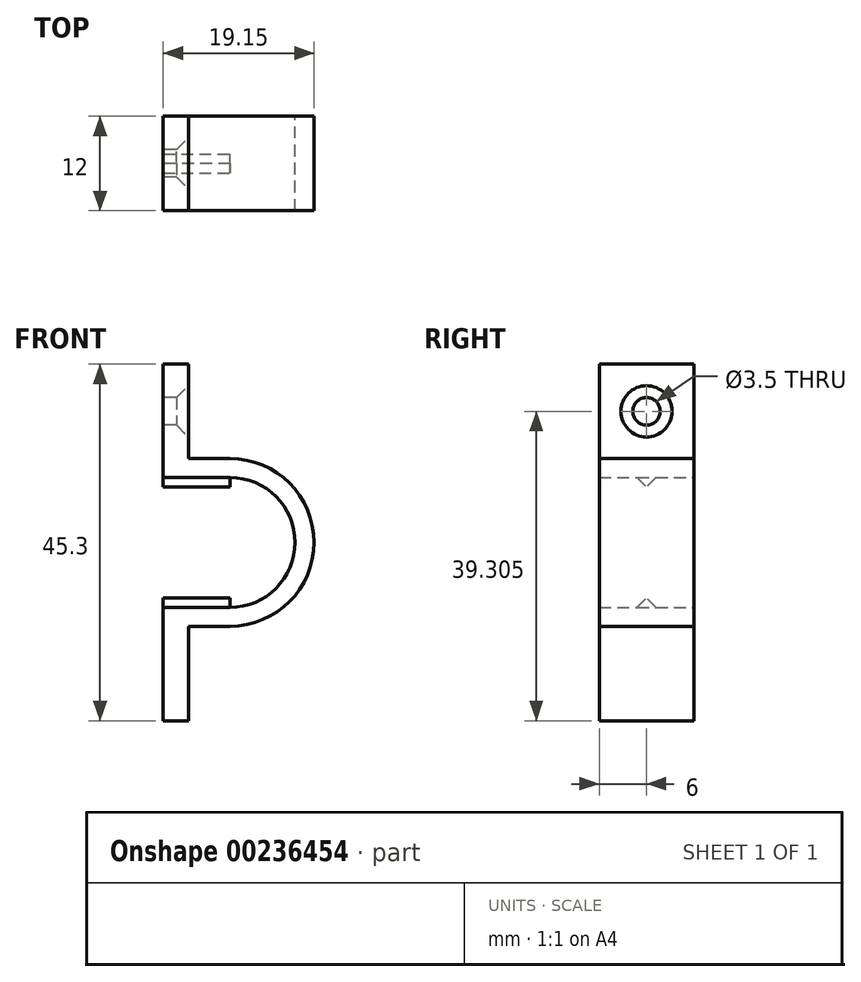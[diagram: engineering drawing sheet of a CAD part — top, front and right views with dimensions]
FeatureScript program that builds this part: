
annotation { "Feature Type Name" : "Feature", "Feature Type Description" : "" }
export const myFeature = defineFeature(function(context is Context, id is Id, definition is map)
    precondition{}
    {
        {
            var Q0;
            Q0=qCreatedBy(makeId("Front.planeOp"),FACE);
            var sketch = newSketch(context, id + "F0", { "sketchPlane" : qUnion([Q0])});
            skLineSegment(sketch, "E0.bottom", {"start": v(-39.03, 42) * mm, "end": v(-35.83, 42) * mm});
            skLineSegment(sketch, "E0.top", {"start": v(-39.03, -3.3) * mm, "end": v(-35.83, -3.3) * mm});
            skLineSegment(sketch, "E0.left", {"start": v(-39.03, 42) * mm, "end": v(-39.03, 27.6) * mm});
            skLineSegment(sketch, "E0.right", {"start": v(-35.83, 42) * mm, "end": v(-35.83, 30) * mm});
            skLineSegment(sketch, "E1.trimOffspring", {"start": v(-35.83, 8.7) * mm, "end": v(-35.83, -3.3) * mm});
            skLineSegment(sketch, "E2.trimOffspring", {"start": v(-39.03, 11.1) * mm, "end": v(-39.03, -3.3) * mm});
            skLineSegment(sketch, "E3", {"start": v(-35.83, 30) * mm, "end": v(-30.53, 30) * mm});
            skLineSegment(sketch, "E4", {"start": v(-30.53, 27.6) * mm, "end": v(-39.03, 27.6) * mm});
            skLineSegment(sketch, "E5", {"start": v(-39.03, 11.1) * mm, "end": v(-30.53, 11.1) * mm});
            skLineSegment(sketch, "E6", {"start": v(-30.53, 8.7) * mm, "end": v(-35.83, 8.7) * mm});
            skLineSegment(sketch, "E7", {"start": v(-30.53, 27.6) * mm, "end": v(-30.53, 11.1) * mm, "construction": true});
            skArc(sketch, "E8", {"start": v(-30.53, 11.1) * mm, "mid": v(-22.28, 19.34) * mm, "end": v(-30.53, 27.6) * mm});
            skArc(sketch, "E9", {"start": v(-30.53, 8.7) * mm, "mid": v(-19.88, 19.34) * mm, "end": v(-30.53, 30) * mm});
            skSolve(sketch);
        }
        {
            var Q0;
            Q0=makeQuery(id+"F0.imprint","IMPRINT",FACE,{"disambiguationData":[TD([[makeQuery(id+"F0.imprint","IMPRINT",EDGE,{"derivedFrom":sQuery(id+"F0.wireOp",EDGE,"E0.bottom")}),-1.0]])]});
            extrude(context, id + "F1", {"entities" : qUnion([Q0]), "depth" : 12 * mm});
        }
        {
            var Q0;
            Q0=makeQuery(id+"F1.opExtrude","SWEPT_FACE",FACE,{"disambiguationData":[OSD([sQuery(id+"F0.wireOp",EDGE,"E0.left")])]});
            var sketch = newSketch(context, id + "F2", { "sketchPlane" : qUnion([Q0])});
            skCircle(sketch, "E10", {"center": v(6, 36) * mm, "radius": 1.75 * mm});
            skLineSegment(sketch, "E11.0.0", {"start": v(0, 11.1) * mm, "end": v(0, 27.6) * mm, "construction": true});
            skLineSegment(sketch, "E11.0.1", {"start": v(0, 11.1) * mm, "end": v(12, 11.1) * mm, "construction": true});
            skLineSegment(sketch, "E11.0.2", {"start": v(12, 11.1) * mm, "end": v(12, 27.6) * mm, "construction": true});
            skLineSegment(sketch, "E11.0.3", {"start": v(12, 27.6) * mm, "end": v(0, 27.6) * mm, "construction": true});
            skLineSegment(sketch, "E12", {"start": v(0, 19.34) * mm, "end": v(12, 19.34) * mm, "construction": true});
            skCircle(sketch, "E13.MirrorC", {"center": v(6, 2.7) * mm, "radius": 1.75 * mm});
            skSolve(sketch);
        }
        {
            var Q0;
            Q0=makeQuery(id+"F2.imprint","IMPRINT",FACE,{"disambiguationData":[TD([[makeQuery(id+"F2.imprint","IMPRINT",EDGE,{"derivedFrom":sQuery(id+"F2.wireOp",EDGE,"E10")}),1.0]])]});
            var Q1;
            Q1=makeQuery(id+"F2.imprint","IMPRINT",FACE,{"disambiguationData":[TD([[makeQuery(id+"F2.imprint","IMPRINT",EDGE,{"derivedFrom":sQuery(id+"F2.wireOp",EDGE,"E13.MirrorC")}),-1.0]])]});
            extrude(context, id + "F3", {"entities" : qUnion([Q0, Q1]), "operationType" : NewBodyOperationType.REMOVE, "endBound" : BoundingType.THROUGH_ALL, "oppositeDirection" : true, "depth" : 25 * mm});
        }
        {
            var Q0;
            Q0=makeQuery(id+"F3.boolean.opBoolean","INTERSECT",EDGE,{"derivedFrom":[makeQuery(id+"F1.opExtrude","SWEPT_FACE",FACE,{"disambiguationData":[OSD([sQuery(id+"F0.wireOp",EDGE,"E0.right")])]}),makeQuery(id+"F3.opExtrude","SWEPT_FACE",FACE,{"disambiguationData":[OSD([sQuery(id+"F2.wireOp",EDGE,"E10")])]})]});
            var Q1;
            Q1=makeQuery(id+"F3.boolean.opBoolean","INTERSECT",EDGE,{"derivedFrom":[makeQuery(id+"F1.opExtrude","SWEPT_FACE",FACE,{"disambiguationData":[OSD([sQuery(id+"F0.wireOp",EDGE,"E1.trimOffspring")])]}),makeQuery(id+"F3.opExtrude","SWEPT_FACE",FACE,{"disambiguationData":[OSD([sQuery(id+"F2.wireOp",EDGE,"E13.MirrorC")])]})]});
            chamfer(context, id + "F4", {"entities" : qUnion([Q0, Q1]), "width" : 1.5 * mm, "tangentPropagation" : true});
        }
        {
            var Q0;
            Q0=makeQuery(id+"F1.opExtrude","SWEPT_FACE",FACE,{"disambiguationData":[OSD([sQuery(id+"F0.wireOp",EDGE,"E5")])]});
            var sketch = newSketch(context, id + "F5", { "sketchPlane" : qUnion([Q0])});
            skLineSegment(sketch, "E14", {"start": v(-30.53, -6) * mm, "end": v(-39.03, -6) * mm, "construction": true});
            skLineSegment(sketch, "E15.bottom", {"start": v(-39.03, -7.2) * mm, "end": v(-30.53, -7.2) * mm});
            skLineSegment(sketch, "E15.top", {"start": v(-39.03, -4.8) * mm, "end": v(-30.53, -4.8) * mm});
            skLineSegment(sketch, "E15.left", {"start": v(-39.03, -7.2) * mm, "end": v(-39.03, -4.8) * mm});
            skPoint(sketch, "E15.middle", {"position": v(-30.53, -6) * mm});
            skLineSegment(sketch, "E16", {"start": v(-30.53, -4.8) * mm, "end": v(-30.53, -7.2) * mm});
            skPoint(sketch, "E15.right.end.orphan", {"position": v(-22.03, -4.8) * mm});
            skPoint(sketch, "E17.orphan", {"position": v(-22.03, -7.2) * mm});
            skSolve(sketch);
        }
        {
            var Q0;
            {var subQ0=sQuery(id+"F5.wireOp",EDGE,"E15.left");Q0=makeQuery(id+"F5.imprint","IMPRINT",FACE,{"disambiguationData":[TD([[makeQuery(id+"F5.imprint","IMPRINT",EDGE,{"derivedFrom":subQ0}),-1.0]])]});}
            extrude(context, id + "F6", {"entities" : qUnion([Q0]), "operationType" : NewBodyOperationType.ADD, "depth" : 1.2 * mm});
        }
        {
            var Q0;
            Q0=makeQuery(id+"F1.opExtrude","SWEPT_FACE",FACE,{"disambiguationData":[OSD([sQuery(id+"F0.wireOp",EDGE,"E4")])]});
            var sketch = newSketch(context, id + "F7", { "sketchPlane" : qUnion([Q0])});
            skLineSegment(sketch, "E18.bottom", {"start": v(-39.03, 4.8) * mm, "end": v(-30.53, 4.8) * mm});
            skLineSegment(sketch, "E18.top", {"start": v(-39.03, 7.2) * mm, "end": v(-30.53, 7.2) * mm});
            skLineSegment(sketch, "E18.left", {"start": v(-39.03, 4.8) * mm, "end": v(-39.03, 7.2) * mm});
            skPoint(sketch, "E18.middle", {"position": v(-30.53, 6) * mm});
            skLineSegment(sketch, "E19", {"start": v(-30.53, 7.2) * mm, "end": v(-30.53, 4.8) * mm});
            skPoint(sketch, "E18.right.end.orphan", {"position": v(-22.03, 7.2) * mm});
            skPoint(sketch, "E18.right.start.orphan", {"position": v(-22.03, 4.8) * mm});
            skSolve(sketch);
        }
        {
            var Q0;
            Q0=makeQuery(id+"F7.imprint","IMPRINT",FACE,{"disambiguationData":[TD([[makeQuery(id+"F7.imprint","IMPRINT",EDGE,{"derivedFrom":sQuery(id+"F7.wireOp",EDGE,"E18.bottom")}),1.0]])]});
            extrude(context, id + "F8", {"entities" : qUnion([Q0]), "operationType" : NewBodyOperationType.ADD, "depth" : 1.2 * mm});
        }
        {
            var Q0;
            Q0=makeQuery(id+"F6.opExtrude","CAP_EDGE",EDGE,{"disambiguationData":[OSD([sQuery(id+"F5.wireOp",EDGE,"E15.bottom")])],"isStart":false});
            var Q1;
            Q1=makeQuery(id+"F6.opExtrude","CAP_EDGE",EDGE,{"disambiguationData":[OSD([sQuery(id+"F5.wireOp",EDGE,"E15.top")])],"isStart":false});
            var Q2;
            Q2=makeQuery(id+"F8.opExtrude","CAP_EDGE",EDGE,{"disambiguationData":[OSD([sQuery(id+"F7.wireOp",EDGE,"E18.top")])],"isStart":false});
            var Q3;
            Q3=makeQuery(id+"F8.opExtrude","CAP_EDGE",EDGE,{"disambiguationData":[OSD([sQuery(id+"F7.wireOp",EDGE,"E18.bottom")])],"isStart":false});
            chamfer(context, id + "F9", {"entities" : qUnion([Q0, Q1, Q2, Q3]), "width" : 1.2 * mm, "tangentPropagation" : true});
        }
    });
